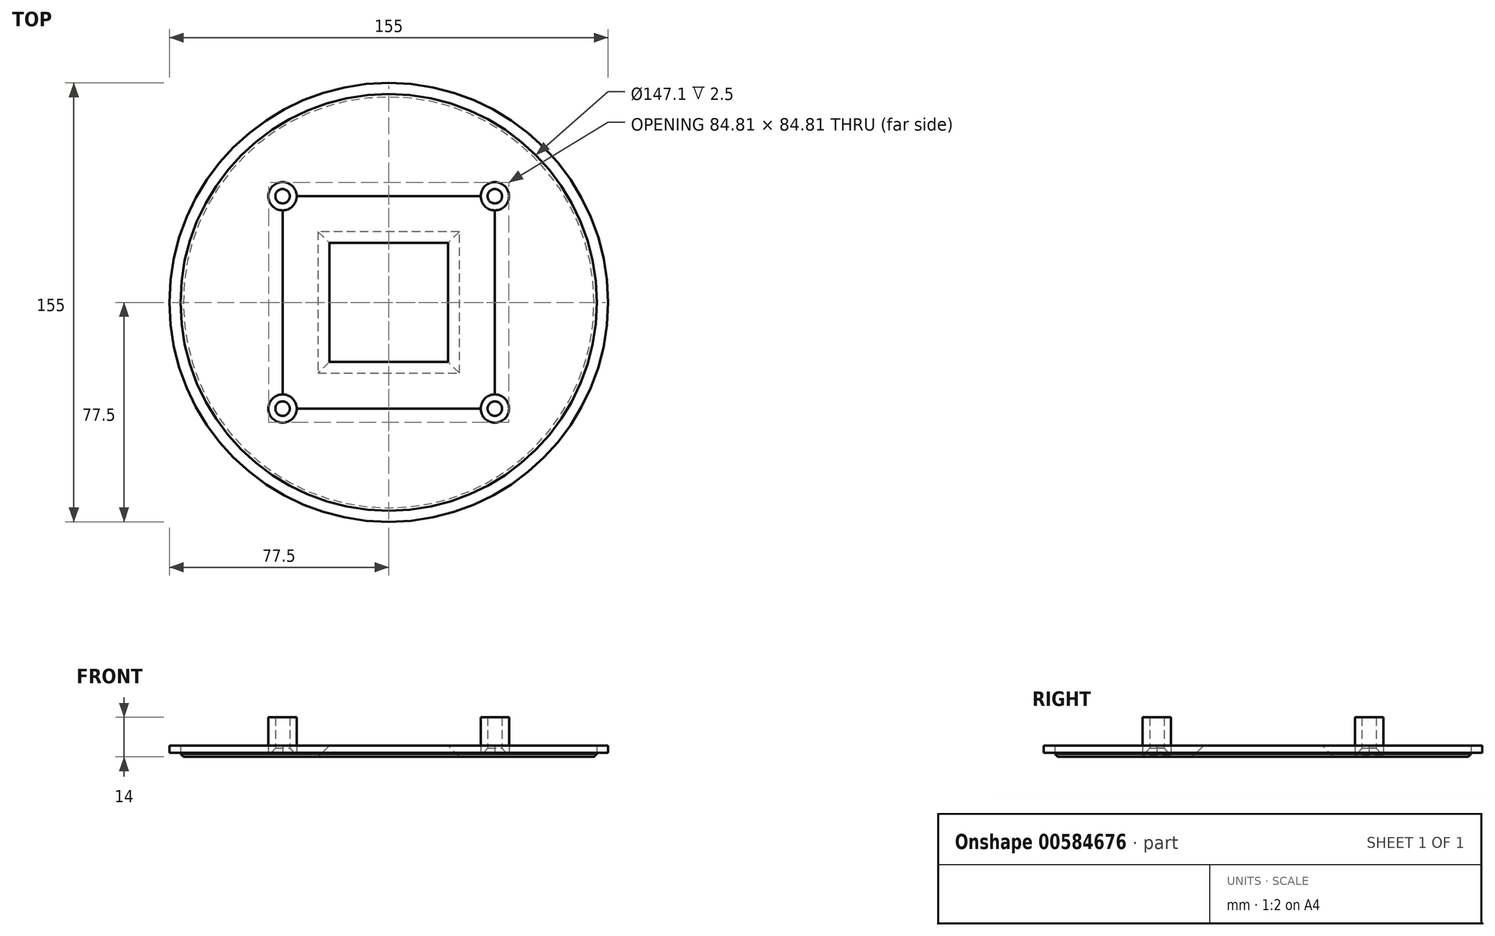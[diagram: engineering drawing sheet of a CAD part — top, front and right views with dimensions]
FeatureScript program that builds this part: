
annotation { "Feature Type Name" : "Feature", "Feature Type Description" : "" }
export const myFeature = defineFeature(function(context is Context, id is Id, definition is map)
    precondition{}
    {
        {
            var Q0;
            Q0=qCreatedBy(makeId("Top.planeOp"),FACE);
            var sketch = newSketch(context, id + "F0", { "sketchPlane" : qUnion([Q0])});
            skCircle(sketch, "E0", {"center": v(0, 0) * mm, "radius": 73.55 * mm});
            skLineSegment(sketch, "E1.bottom", {"start": v(37.5, 37.5) * mm, "end": v(-37.5, 37.5) * mm});
            skLineSegment(sketch, "E1.top", {"start": v(37.5, -37.5) * mm, "end": v(-37.5, -37.5) * mm});
            skLineSegment(sketch, "E1.left", {"start": v(37.5, 37.5) * mm, "end": v(37.5, -37.5) * mm});
            skLineSegment(sketch, "E1.right", {"start": v(-37.5, 37.5) * mm, "end": v(-37.5, -37.5) * mm});
            skPoint(sketch, "E2", {"position": v(-37.5, 37.5) * mm});
            skPoint(sketch, "E3", {"position": v(37.5, 37.5) * mm});
            skPoint(sketch, "E4", {"position": v(37.5, -37.5) * mm});
            skPoint(sketch, "E5", {"position": v(-37.5, -37.5) * mm});
            skLineSegment(sketch, "E6.bottom", {"start": v(20, -20) * mm, "end": v(-20, -20) * mm});
            skLineSegment(sketch, "E6.top", {"start": v(20, 20) * mm, "end": v(-20, 20) * mm});
            skLineSegment(sketch, "E6.left", {"start": v(20, -20) * mm, "end": v(20, 20) * mm});
            skLineSegment(sketch, "E6.right", {"start": v(-20, -20) * mm, "end": v(-20, 20) * mm});
            skPoint(sketch, "E7", {"position": v(-20, 20) * mm});
            skPoint(sketch, "E8", {"position": v(20, 20) * mm});
            skPoint(sketch, "E9", {"position": v(20, -20) * mm});
            skPoint(sketch, "E10", {"position": v(-20, -20) * mm});
            skCircle(sketch, "E11", {"center": v(0, 0) * mm, "radius": 77.5 * mm});
            skCircle(sketch, "E12", {"center": v(-37.5, -37.5) * mm, "radius": 5 * mm});
            skCircle(sketch, "E13", {"center": v(37.5, -37.5) * mm, "radius": 5 * mm});
            skCircle(sketch, "E14", {"center": v(37.5, 37.5) * mm, "radius": 5 * mm});
            skCircle(sketch, "E15", {"center": v(-37.5, 37.5) * mm, "radius": 5 * mm});
            skSolve(sketch);
        }
        {
            var Q0;
            {var subQ0=sQuery(id+"F0.wireOp",EDGE,"E1.right");var subQ1=sQuery(id+"F0.wireOp",EDGE,"E1.top");var subQ2=makeQuery(id+"F0.imprint","INTERSECT",VERTEX,{"derivedFrom":[subQ1,subQ0]});Q0=makeQuery(id+"F0.imprint","IMPRINT",FACE,{"disambiguationData":[TD([[makeQuery(id+"F0.imprint","IMPRINT",EDGE,{"disambiguationData":[TD([[subQ2,1.0]])],"derivedFrom":subQ1}),-1.0]])]});}
            var Q1;
            {var subQ0=sQuery(id+"F0.wireOp",EDGE,"E1.right");var subQ1=sQuery(id+"F0.wireOp",EDGE,"E1.top");var subQ2=makeQuery(id+"F0.imprint","INTERSECT",VERTEX,{"derivedFrom":[subQ1,subQ0]});Q1=makeQuery(id+"F0.imprint","IMPRINT",FACE,{"disambiguationData":[TD([[makeQuery(id+"F0.imprint","IMPRINT",EDGE,{"disambiguationData":[TD([[subQ2,1.0]])],"derivedFrom":subQ1}),1.0]])]});}
            var Q2;
            {var subQ0=sQuery(id+"F0.wireOp",EDGE,"E1.right");var subQ1=sQuery(id+"F0.wireOp",EDGE,"E1.bottom");var subQ2=makeQuery(id+"F0.imprint","INTERSECT",VERTEX,{"derivedFrom":[subQ1,subQ0]});Q2=makeQuery(id+"F0.imprint","IMPRINT",FACE,{"disambiguationData":[TD([[makeQuery(id+"F0.imprint","IMPRINT",EDGE,{"disambiguationData":[TD([[subQ2,1.0]])],"derivedFrom":subQ1}),1.0]])]});}
            var Q3;
            {var subQ0=sQuery(id+"F0.wireOp",EDGE,"E1.right");var subQ1=sQuery(id+"F0.wireOp",EDGE,"E1.bottom");var subQ2=makeQuery(id+"F0.imprint","INTERSECT",VERTEX,{"derivedFrom":[subQ1,subQ0]});Q3=makeQuery(id+"F0.imprint","IMPRINT",FACE,{"disambiguationData":[TD([[makeQuery(id+"F0.imprint","IMPRINT",EDGE,{"disambiguationData":[TD([[subQ2,1.0]])],"derivedFrom":subQ1}),-1.0]])]});}
            var Q4;
            {var subQ0=sQuery(id+"F0.wireOp",EDGE,"E1.left");var subQ1=sQuery(id+"F0.wireOp",EDGE,"E1.top");var subQ2=makeQuery(id+"F0.imprint","INTERSECT",VERTEX,{"derivedFrom":[subQ1,subQ0]});Q4=makeQuery(id+"F0.imprint","IMPRINT",FACE,{"disambiguationData":[TD([[makeQuery(id+"F0.imprint","IMPRINT",EDGE,{"disambiguationData":[TD([[subQ2,-1.0]])],"derivedFrom":subQ1}),-1.0]])]});}
            var Q5;
            {var subQ0=sQuery(id+"F0.wireOp",EDGE,"E1.left");var subQ1=sQuery(id+"F0.wireOp",EDGE,"E1.top");var subQ2=makeQuery(id+"F0.imprint","INTERSECT",VERTEX,{"derivedFrom":[subQ1,subQ0]});Q5=makeQuery(id+"F0.imprint","IMPRINT",FACE,{"disambiguationData":[TD([[makeQuery(id+"F0.imprint","IMPRINT",EDGE,{"disambiguationData":[TD([[subQ2,-1.0]])],"derivedFrom":subQ1}),1.0]])]});}
            var Q6;
            {var subQ0=sQuery(id+"F0.wireOp",EDGE,"E1.left");var subQ1=sQuery(id+"F0.wireOp",EDGE,"E1.bottom");var subQ2=makeQuery(id+"F0.imprint","INTERSECT",VERTEX,{"derivedFrom":[subQ1,subQ0]});Q6=makeQuery(id+"F0.imprint","IMPRINT",FACE,{"disambiguationData":[TD([[makeQuery(id+"F0.imprint","IMPRINT",EDGE,{"disambiguationData":[TD([[subQ2,-1.0]])],"derivedFrom":subQ1}),1.0]])]});}
            var Q7;
            {var subQ0=sQuery(id+"F0.wireOp",EDGE,"E1.left");var subQ1=sQuery(id+"F0.wireOp",EDGE,"E1.bottom");var subQ2=makeQuery(id+"F0.imprint","INTERSECT",VERTEX,{"derivedFrom":[subQ1,subQ0]});Q7=makeQuery(id+"F0.imprint","IMPRINT",FACE,{"disambiguationData":[TD([[makeQuery(id+"F0.imprint","IMPRINT",EDGE,{"disambiguationData":[TD([[subQ2,-1.0]])],"derivedFrom":subQ1}),-1.0]])]});}
            extrude(context, id + "F1", {"entities" : qUnion([Q0, Q1, Q2, Q3, Q4, Q5, Q6, Q7]), "depth" : 14 * mm, "offsetDistance" : 25 * mm});
        }
        {
            var Q0;
            Q0=makeQuery(id+"F0.imprint","IMPRINT",FACE,{"disambiguationData":[TD([[makeQuery(id+"F0.imprint","IMPRINT",EDGE,{"derivedFrom":sQuery(id+"F0.wireOp",EDGE,"E6.bottom")}),1.0]])]});
            extrude(context, id + "F2", {"entities" : qUnion([Q0]), "depth" : 4 * mm, "offsetDistance" : 25 * mm});
        }
        {
            var Q0;
            Q0=makeQuery(id+"F0.imprint","IMPRINT",FACE,{"disambiguationData":[TD([[makeQuery(id+"F0.imprint","IMPRINT",EDGE,{"derivedFrom":sQuery(id+"F0.wireOp",EDGE,"E0")}),-1.0]])]});
            extrude(context, id + "F3", {"entities" : qUnion([Q0]), "depth" : 4 * mm, "offsetDistance" : 25 * mm});
        }
        {
            var Q0;
            Q0=makeQuery(id+"F0.imprint","IMPRINT",FACE,{"disambiguationData":[TD([[makeQuery(id+"F0.imprint","IMPRINT",EDGE,{"derivedFrom":sQuery(id+"F0.wireOp",EDGE,"E0")}),1.0]])]});
            extrude(context, id + "F4", {"entities" : qUnion([Q0]), "depth" : 4 * mm, "offsetDistance" : 25 * mm});
        }
        {
            var Q0;
            Q0=makeQuery(id+"F0.imprint","IMPRINT",FACE,{"disambiguationData":[TD([[makeQuery(id+"F0.imprint","IMPRINT",EDGE,{"derivedFrom":sQuery(id+"F0.wireOp",EDGE,"E0")}),-1.0]])]});
            extrude(context, id + "F5", {"entities" : qUnion([Q0]), "operationType" : NewBodyOperationType.REMOVE, "depth" : 1.5 * mm, "offsetDistance" : 25 * mm});
        }
        {
            var Q0;
            Q0=sQuery(id+"F0.wireOp",VERTEX,"E2");
            var Q1;
            Q1=sQuery(id+"F0.wireOp",VERTEX,"E3");
            var Q2;
            Q2=sQuery(id+"F0.wireOp",VERTEX,"E1.left.end");
            var Q3;
            Q3=sQuery(id+"F0.wireOp",VERTEX,"E5");
            var Q4;
            Q4=makeQuery(id+"F1.opExtrude","SWEPT_BODY",BODY,{"disambiguationData":[OSD([sQuery(id+"F0.wireOp",EDGE,"E15")])]});
            var Q5;
            Q5=makeQuery(id+"F1.opExtrude","SWEPT_BODY",BODY,{"disambiguationData":[OSD([sQuery(id+"F0.wireOp",EDGE,"E14")])]});
            var Q6;
            Q6=makeQuery(id+"F1.opExtrude","SWEPT_BODY",BODY,{"disambiguationData":[OSD([sQuery(id+"F0.wireOp",EDGE,"E13")])]});
            var Q7;
            Q7=makeQuery(id+"F1.opExtrude","SWEPT_BODY",BODY,{"disambiguationData":[OSD([sQuery(id+"F0.wireOp",EDGE,"E12")])]});
            hole(context, id + "F6", {"style" : HoleStyle.C_SINK, "endStyle" : HoleEndStyle.THROUGH, "oppositeDirection" : true, "standardTappedOrClearance" : lookupTablePath({ "standard" : "ANSI", "fit" : "Normal (ASME)", "size" : "#10", "type" : "Clearance" }), "standardBlindInLast" : lookupTablePath({ "fit" : "Free", "standard" : "ANSI", "size" : "#10", "type" : "Clearance" }), "holeDiameter" : 5.1 * mm, "cSinkDiameter" : 10.44 * mm, "cSinkAngle" : 82 * degree, "majorDiameter" : 5 * mm, "isTappedThrough" : true, "tappedDepth" : 12 * mm, "tapClearance" : 3, "startFromSketch" : true, "locations" : qUnion([Q0, Q1, Q2, Q3]), "scope" : qUnion([Q4, Q5, Q6, Q7])});
        }
        {
            var Q0;
            Q0=makeQuery(id+"F2.opExtrude","CAP_EDGE",EDGE,{"disambiguationData":[OSD([sQuery(id+"F0.wireOp",EDGE,"E6.bottom")])],"isStart":true});
            var Q1;
            Q1=makeQuery(id+"F2.opExtrude","CAP_EDGE",EDGE,{"disambiguationData":[OSD([sQuery(id+"F0.wireOp",EDGE,"E6.left")])],"isStart":true});
            var Q2;
            Q2=makeQuery(id+"F2.opExtrude","CAP_EDGE",EDGE,{"disambiguationData":[OSD([sQuery(id+"F0.wireOp",EDGE,"E6.top")])],"isStart":true});
            var Q3;
            Q3=makeQuery(id+"F2.opExtrude","CAP_EDGE",EDGE,{"disambiguationData":[OSD([sQuery(id+"F0.wireOp",EDGE,"E6.right")])],"isStart":true});
            chamfer(context, id + "F7", {"entities" : qUnion([Q0, Q1, Q2, Q3]), "width" : 5 * mm, "tangentPropagation" : true});
        }
        {
            var Q0;
            Q0=makeQuery(id+"F4.opExtrude","CAP_EDGE",EDGE,{"disambiguationData":[OSD([sQuery(id+"F0.wireOp",EDGE,"E0")])],"isStart":true});
            chamfer(context, id + "F8", {"entities" : qUnion([Q0]), "width" : 1 * mm, "tangentPropagation" : true});
        }
    });
